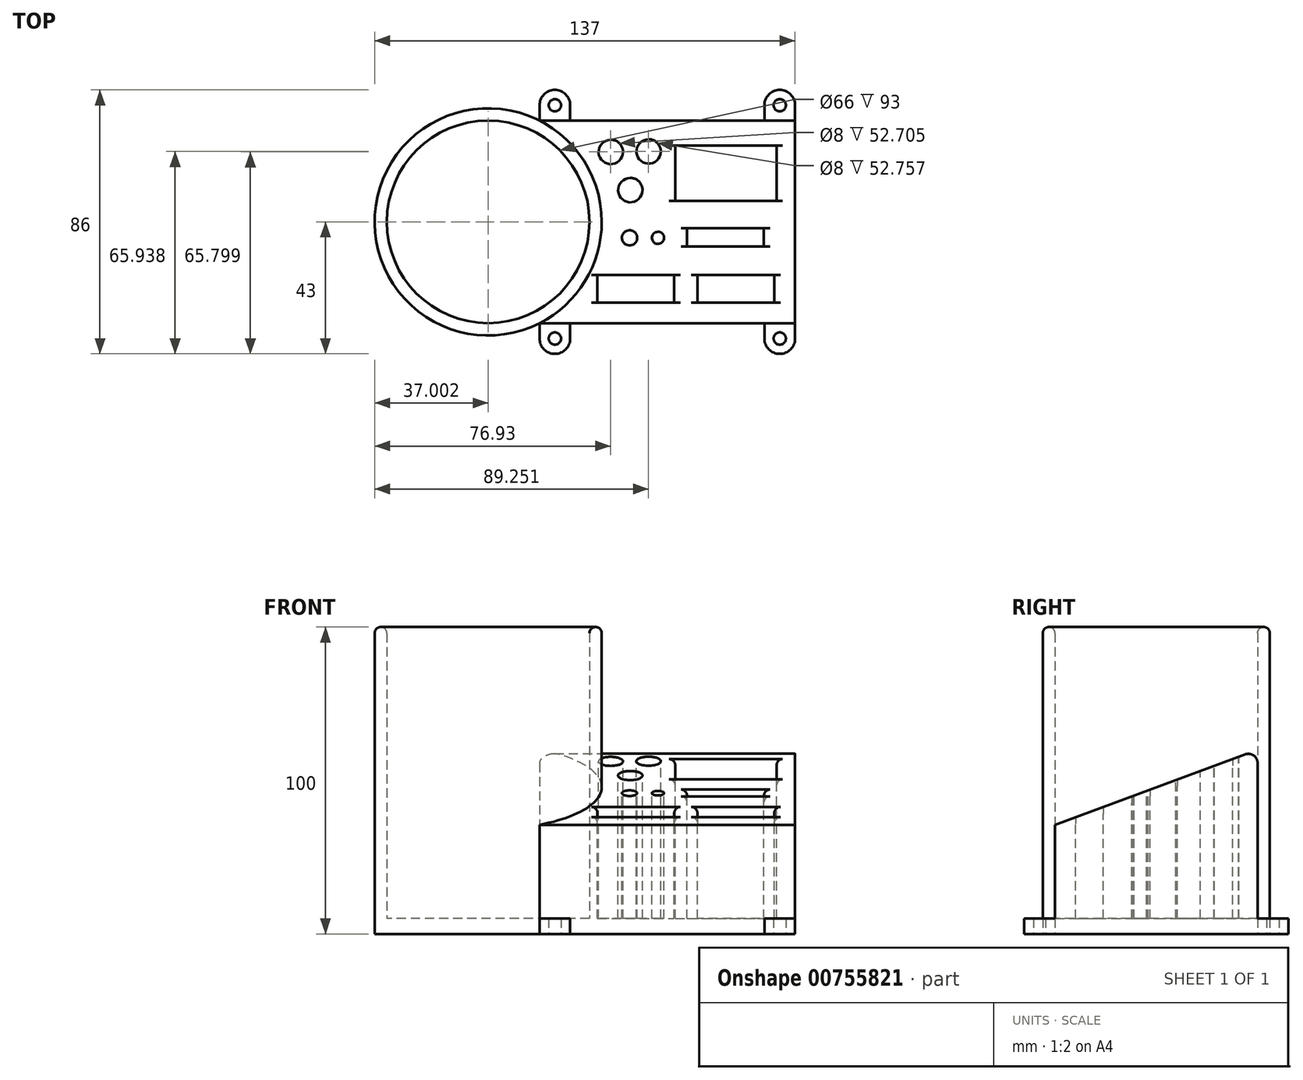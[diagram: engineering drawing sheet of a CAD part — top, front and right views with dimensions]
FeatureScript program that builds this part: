
annotation { "Feature Type Name" : "Feature", "Feature Type Description" : "" }
export const myFeature = defineFeature(function(context is Context, id is Id, definition is map)
    precondition{}
    {
        {
            var Q0;
            Q0=qCreatedBy(makeId("Top.planeOp"),FACE);
            var sketch = newSketch(context, id + "F0", { "sketchPlane" : qUnion([Q0])});
            skCircle(sketch, "E0", {"center": v(-81.99, 0) * mm, "radius": 33 * mm});
            skCircle(sketch, "E1", {"center": v(-81.99, 0) * mm, "radius": 37 * mm});
            skLineSegment(sketch, "E2.bottom", {"start": v(-81.99, 33) * mm, "end": v(18.01, 33) * mm});
            skLineSegment(sketch, "E2.top", {"start": v(-81.99, -33) * mm, "end": v(18.01, -33) * mm});
            skLineSegment(sketch, "E2.left", {"start": v(-81.99, 33) * mm, "end": v(-81.99, -33) * mm});
            skLineSegment(sketch, "E2.right", {"start": v(18.01, 33) * mm, "end": v(18.01, -33) * mm});
            skSolve(sketch);
        }
        {
            var Q0;
            {var subQ1=sQuery(id+"F0.wireOp",EDGE,"E2.bottom");var subQ6=sQuery(id+"F0.wireOp",EDGE,"E1");var subQ7=makeQuery(id+"F0.imprint","INTERSECT",VERTEX,{"derivedFrom":[subQ6,subQ1]});Q0=makeQuery(id+"F0.imprint","IMPRINT",FACE,{"disambiguationData":[TD([[makeQuery(id+"F0.imprint","IMPRINT",EDGE,{"disambiguationData":[TD([[subQ7,-1.0]])],"derivedFrom":subQ6}),1.0]])]});}
            var Q1;
            {var subQ1=sQuery(id+"F0.wireOp",EDGE,"E2.bottom");var subQ6=sQuery(id+"F0.wireOp",EDGE,"E1");var subQ8=makeQuery(id+"F0.imprint","INTERSECT",VERTEX,{"derivedFrom":[subQ6,subQ1]});Q1=makeQuery(id+"F0.imprint","IMPRINT",FACE,{"disambiguationData":[TD([[makeQuery(id+"F0.imprint","IMPRINT",EDGE,{"disambiguationData":[TD([[subQ8,1.0]])],"derivedFrom":subQ6}),1.0]])]});}
            extrude(context, id + "F1", {"entities" : qUnion([Q0, Q1]), "depth" : 100 * mm, "offsetDistance" : 25 * mm});
        }
        {
            var Q0;
            Q0 = qSketchRegion(id + "F0", true);
            extrude(context, id + "F2", {"entities" : qUnion([Q0]), "operationType" : NewBodyOperationType.ADD, "depth" : 60 * mm, "offsetDistance" : 25 * mm});
        }
        {
            var Q0;
            {var subQ0=sQuery(id+"F0.wireOp",EDGE,"E1");var subQ1=sQuery(id+"F0.wireOp",EDGE,"E0");Q0=makeQuery(id+"F2.boolean.opBoolean","MERGE",FACE,{"derivedFrom":[makeQuery(id+"F1.opExtrude","CAP_FACE",FACE,{"disambiguationData":[OSD([subQ1,subQ0])],"isStart":true}),makeQuery(id+"F2.opExtrude","CAP_FACE",FACE,{"disambiguationData":[OSD([subQ1,subQ0,sQuery(id+"F0.wireOp",EDGE,"E2.bottom"),sQuery(id+"F0.wireOp",EDGE,"E2.top"),sQuery(id+"F0.wireOp",EDGE,"E2.right")])],"isStart":true})]});}
            var sketch = newSketch(context, id + "F3", { "sketchPlane" : qUnion([Q0])});
            skCircle(sketch, "E3", {"center": v(-81.99, 0) * mm, "radius": 33 * mm});
            skSolve(sketch);
        }
        {
            var Q0;
            Q0 = qSketchRegion(id + "F3", true);
            extrude(context, id + "F4", {"entities" : qUnion([Q0]), "operationType" : NewBodyOperationType.ADD, "oppositeDirection" : true, "depth" : 5 * mm, "offsetDistance" : 25 * mm});
        }
        {
            var Q0;
            Q0=makeQuery(id+"F2.opExtrude","CAP_FACE",FACE,{"disambiguationData":[OSD([sQuery(id+"F0.wireOp",EDGE,"E0"),sQuery(id+"F0.wireOp",EDGE,"E1"),sQuery(id+"F0.wireOp",EDGE,"E2.bottom"),sQuery(id+"F0.wireOp",EDGE,"E2.top"),sQuery(id+"F0.wireOp",EDGE,"E2.right")])],"isStart":false});
            var sketch = newSketch(context, id + "F5", { "sketchPlane" : qUnion([Q0])});
            skLineSegment(sketch, "E4.bottom", {"start": v(-21.04, 24.86) * mm, "end": v(11.96, 24.86) * mm});
            skLineSegment(sketch, "E4.top", {"start": v(-21.04, 6.86) * mm, "end": v(11.96, 6.86) * mm});
            skLineSegment(sketch, "E4.left", {"start": v(-21.04, 24.86) * mm, "end": v(-21.04, 6.86) * mm});
            skLineSegment(sketch, "E4.right", {"start": v(11.96, 24.86) * mm, "end": v(11.96, 6.86) * mm});
            skCircle(sketch, "E5", {"center": v(-35.93, -5.2) * mm, "radius": 2.5 * mm});
            skCircle(sketch, "E6", {"center": v(-26.66, -5.2) * mm, "radius": 2 * mm});
            skPoint(sketch, "E7.firstSnap0", {"position": v(-4.54, 6.86) * mm});
            skLineSegment(sketch, "E7.right", {"start": v(7.83, -2.02) * mm, "end": v(7.83, -8.02) * mm});
            skLineSegment(sketch, "E8.MirrorCS", {"start": v(-17.17, -2.02) * mm, "end": v(-17.17, -8.02) * mm});
            skLineSegment(sketch, "E9", {"start": v(-17.17, -2.02) * mm, "end": v(7.83, -2.02) * mm});
            skLineSegment(sketch, "E10", {"start": v(-17.17, -8.02) * mm, "end": v(7.83, -8.02) * mm});
            skLineSegment(sketch, "E11.bottom", {"start": v(-46.37, -17.29) * mm, "end": v(-21.37, -17.29) * mm});
            skLineSegment(sketch, "E11.top", {"start": v(-46.37, -26.29) * mm, "end": v(-21.37, -26.29) * mm});
            skLineSegment(sketch, "E11.left", {"start": v(-46.37, -17.29) * mm, "end": v(-46.37, -26.29) * mm});
            skLineSegment(sketch, "E11.right", {"start": v(-21.37, -17.29) * mm, "end": v(-21.37, -26.29) * mm});
            skCircle(sketch, "E12", {"center": v(-42.06, 22.8) * mm, "radius": 4 * mm});
            skCircle(sketch, "E13", {"center": v(-29.74, 22.94) * mm, "radius": 4 * mm});
            skCircle(sketch, "E14", {"center": v(-35.7, 10.35) * mm, "radius": 4 * mm});
            skLineSegment(sketch, "E15.bottom", {"start": v(11.21, -26.29) * mm, "end": v(-13.79, -26.29) * mm});
            skLineSegment(sketch, "E15.top", {"start": v(11.21, -17.29) * mm, "end": v(-13.79, -17.29) * mm});
            skLineSegment(sketch, "E15.left", {"start": v(11.21, -26.29) * mm, "end": v(11.21, -17.29) * mm});
            skLineSegment(sketch, "E15.right", {"start": v(-13.79, -26.29) * mm, "end": v(-13.79, -17.29) * mm});
            skPoint(sketch, "E15.middle", {"position": v(-1.29, -21.79) * mm});
            skPoint(sketch, "E15.middle.positionSnap0", {"position": v(-46.37, -21.79) * mm});
            skPoint(sketch, "E15.cornerSnap0", {"position": v(-33.87, -26.29) * mm});
            skPoint(sketch, "E15.centerSnap0", {"position": v(-46.37, -21.79) * mm});
            skSolve(sketch);
        }
        {
            var Q0;
            Q0 = qSketchRegion(id + "F5", true);
            extrude(context, id + "F6", {"entities" : qUnion([Q0]), "operationType" : NewBodyOperationType.REMOVE, "oppositeDirection" : true, "depth" : 55 * mm, "offsetDistance" : 25 * mm});
        }
        {
            var Q0;
            Q0=makeQuery(id+"F2.opExtrude","SWEPT_FACE",FACE,{"disambiguationData":[OSD([sQuery(id+"F0.wireOp",EDGE,"E2.right")])]});
            var sketch = newSketch(context, id + "F7", { "sketchPlane" : qUnion([Q0])});
            skLineSegment(sketch, "E16", {"start": v(33, 60) * mm, "end": v(-33, 35.57) * mm});
            skLineSegment(sketch, "E17", {"start": v(-33, 35.57) * mm, "end": v(-33, 60) * mm});
            skLineSegment(sketch, "E18", {"start": v(-33, 60) * mm, "end": v(33, 60) * mm});
            skSolve(sketch);
        }
        {
            var Q0;
            Q0 = qSketchRegion(id + "F7", true);
            extrude(context, id + "F8", {"entities" : qUnion([Q0]), "operationType" : NewBodyOperationType.REMOVE, "oppositeDirection" : true, "depth" : 123.5 * mm, "offsetDistance" : 25 * mm});
        }
        {
            var Q0;
            Q0=makeQuery(id+"F1.opExtrude","CAP_FACE",FACE,{"disambiguationData":[OSD([sQuery(id+"F0.wireOp",EDGE,"E0"),sQuery(id+"F0.wireOp",EDGE,"E1")])],"isStart":false});
            extrude(context, id + "F9", {"entities" : qUnion([Q0]), "operationType" : NewBodyOperationType.ADD, "oppositeDirection" : true, "depth" : 100 * mm, "offsetDistance" : 25 * mm});
        }
        {
            var Q0;
            {var subQ0=sQuery(id+"F0.wireOp",EDGE,"E1");var subQ1=sQuery(id+"F0.wireOp",EDGE,"E0");Q0=makeQuery(id+"F4.boolean.opBoolean","MERGE",FACE,{"derivedFrom":[makeQuery(id+"F2.boolean.opBoolean","MERGE",FACE,{"derivedFrom":[makeQuery(id+"F1.opExtrude","CAP_FACE",FACE,{"disambiguationData":[OSD([subQ1,subQ0])],"isStart":true}),makeQuery(id+"F2.opExtrude","CAP_FACE",FACE,{"disambiguationData":[OSD([subQ1,subQ0,sQuery(id+"F0.wireOp",EDGE,"E2.bottom"),sQuery(id+"F0.wireOp",EDGE,"E2.top"),sQuery(id+"F0.wireOp",EDGE,"E2.right")])],"isStart":true})]}),makeQuery(id+"F4.opExtrude","CAP_FACE",FACE,{"disambiguationData":[OSD([sQuery(id+"F3.wireOp",EDGE,"E3")])],"isStart":true})]});}
            var sketch = newSketch(context, id + "F10", { "sketchPlane" : qUnion([Q0])});
            skLineSegment(sketch, "E19.bottom", {"start": v(18.01, 33) * mm, "end": v(8.01, 33) * mm});
            skLineSegment(sketch, "E19.top", {"start": v(18.01, 43) * mm, "end": v(8.01, 43) * mm});
            skLineSegment(sketch, "E19.left", {"start": v(18.01, 33) * mm, "end": v(18.01, 43) * mm});
            skLineSegment(sketch, "E19.right", {"start": v(8.01, 33) * mm, "end": v(8.01, 43) * mm});
            skLineSegment(sketch, "E20.bottom", {"start": v(18.01, -33) * mm, "end": v(8.01, -33) * mm});
            skLineSegment(sketch, "E20.top", {"start": v(18.01, -43) * mm, "end": v(8.01, -43) * mm});
            skLineSegment(sketch, "E20.left", {"start": v(18.01, -33) * mm, "end": v(18.01, -43) * mm});
            skLineSegment(sketch, "E20.right", {"start": v(8.01, -33) * mm, "end": v(8.01, -43) * mm});
            skLineSegment(sketch, "E21.bottom", {"start": v(-65.26, -33) * mm, "end": v(-55.26, -33) * mm});
            skLineSegment(sketch, "E21.top", {"start": v(-65.26, -43) * mm, "end": v(-55.26, -43) * mm});
            skLineSegment(sketch, "E21.left", {"start": v(-65.26, -33) * mm, "end": v(-65.26, -43) * mm});
            skLineSegment(sketch, "E21.right", {"start": v(-55.26, -33) * mm, "end": v(-55.26, -43) * mm});
            skLineSegment(sketch, "E22.bottom", {"start": v(-65.26, 33) * mm, "end": v(-55.26, 33) * mm});
            skLineSegment(sketch, "E22.top", {"start": v(-65.26, 43) * mm, "end": v(-55.26, 43) * mm});
            skLineSegment(sketch, "E22.left", {"start": v(-65.26, 33) * mm, "end": v(-65.26, 43) * mm});
            skLineSegment(sketch, "E22.right", {"start": v(-55.26, 33) * mm, "end": v(-55.26, 43) * mm});
            skCircle(sketch, "E23", {"center": v(-60.26, 38) * mm, "radius": 2 * mm});
            skPoint(sketch, "E23.centerSnap0", {"position": v(-55.26, 38) * mm});
            skPoint(sketch, "E23.centerSnap1", {"position": v(-60.26, 43) * mm});
            skCircle(sketch, "E24", {"center": v(13.01, 38) * mm, "radius": 2 * mm});
            skPoint(sketch, "E24.centerSnap0", {"position": v(13.01, 43) * mm});
            skPoint(sketch, "E24.centerSnap1", {"position": v(-65.26, 38) * mm});
            skCircle(sketch, "E25", {"center": v(13.01, -38) * mm, "radius": 2 * mm});
            skPoint(sketch, "E25.centerSnap0", {"position": v(13.01, -43) * mm});
            skPoint(sketch, "E25.centerSnap1", {"position": v(18.01, -38) * mm});
            skCircle(sketch, "E26", {"center": v(-60.26, -38) * mm, "radius": 2 * mm});
            skPoint(sketch, "E26.centerSnap0", {"position": v(-55.26, -38) * mm});
            skPoint(sketch, "E26.centerSnap1", {"position": v(-60.26, -43) * mm});
            skSolve(sketch);
        }
        {
            var Q0;
            Q0=makeQuery(id+"F1.opExtrude","CAP_EDGE",EDGE,{"disambiguationData":[OSD([sQuery(id+"F0.wireOp",EDGE,"E1")])],"isStart":false});
            var Q1;
            Q1=makeQuery(id+"F1.opExtrude","CAP_EDGE",EDGE,{"disambiguationData":[OSD([sQuery(id+"F0.wireOp",EDGE,"E0")])],"isStart":false});
            fillet(context, id + "F11", {"entities" : qUnion([Q0, Q1]), "radius" : 2 * mm, "tangentPropagation" : true, "allowEdgeOverflow" : false});
        }
        {
            var Q0;
            Q0 = qSketchRegion(id + "F10", true);
            extrude(context, id + "F12", {"entities" : qUnion([Q0]), "operationType" : NewBodyOperationType.ADD, "oppositeDirection" : true, "depth" : 5 * mm, "offsetDistance" : 25 * mm});
        }
        {
            var Q0;
            Q0=makeQuery(id+"F12.opExtrude","SWEPT_EDGE",EDGE,{"disambiguationData":[OSD([sQuery(id+"F10.wireOp",EDGE,"E22.top"),sQuery(id+"F10.wireOp",EDGE,"E22.left")])]});
            var Q1;
            Q1=makeQuery(id+"F12.opExtrude","SWEPT_EDGE",EDGE,{"disambiguationData":[OSD([sQuery(id+"F10.wireOp",EDGE,"E22.top"),sQuery(id+"F10.wireOp",EDGE,"E22.right")])]});
            var Q2;
            Q2=makeQuery(id+"F12.opExtrude","SWEPT_EDGE",EDGE,{"disambiguationData":[OSD([sQuery(id+"F10.wireOp",EDGE,"E19.top"),sQuery(id+"F10.wireOp",EDGE,"E19.right")])]});
            var Q3;
            Q3=makeQuery(id+"F12.opExtrude","SWEPT_EDGE",EDGE,{"disambiguationData":[OSD([sQuery(id+"F10.wireOp",EDGE,"E19.top"),sQuery(id+"F10.wireOp",EDGE,"E19.left")])]});
            var Q4;
            Q4=makeQuery(id+"F12.opExtrude","SWEPT_EDGE",EDGE,{"disambiguationData":[OSD([sQuery(id+"F10.wireOp",EDGE,"E20.top"),sQuery(id+"F10.wireOp",EDGE,"E20.left")])]});
            var Q5;
            Q5=makeQuery(id+"F12.opExtrude","SWEPT_EDGE",EDGE,{"disambiguationData":[OSD([sQuery(id+"F10.wireOp",EDGE,"E20.top"),sQuery(id+"F10.wireOp",EDGE,"E20.right")])]});
            var Q6;
            Q6=makeQuery(id+"F12.opExtrude","SWEPT_EDGE",EDGE,{"disambiguationData":[OSD([sQuery(id+"F10.wireOp",EDGE,"E21.top"),sQuery(id+"F10.wireOp",EDGE,"E21.right")])]});
            var Q7;
            Q7=makeQuery(id+"F12.opExtrude","SWEPT_EDGE",EDGE,{"disambiguationData":[OSD([sQuery(id+"F10.wireOp",EDGE,"E21.top"),sQuery(id+"F10.wireOp",EDGE,"E21.left")])]});
            fillet(context, id + "F13", {"entities" : qUnion([Q0, Q1, Q2, Q3, Q4, Q5, Q6, Q7]), "radius" : 5 * mm, "tangentPropagation" : true, "allowEdgeOverflow" : false});
        }
        {
            var Q0;
            Q0=makeQuery(id+"F8.boolean.opBoolean","INTERSECT",EDGE,{"derivedFrom":[makeQuery(id+"F6.boolean.opBoolean","COPY",FACE,{"derivedFrom":makeQuery(id+"F6.opExtrude","SWEPT_FACE",FACE,{"disambiguationData":[OSD([sQuery(id+"F5.wireOp",EDGE,"E4.left")])]})}),makeQuery(id+"F8.opExtrude","SWEPT_FACE",FACE,{"disambiguationData":[OSD([sQuery(id+"F7.wireOp",EDGE,"E16")])]})]});
            var Q1;
            Q1=makeQuery(id+"F8.boolean.opBoolean","INTERSECT",EDGE,{"derivedFrom":[makeQuery(id+"F6.boolean.opBoolean","COPY",FACE,{"derivedFrom":makeQuery(id+"F6.opExtrude","SWEPT_FACE",FACE,{"disambiguationData":[OSD([sQuery(id+"F5.wireOp",EDGE,"E4.right")])]})}),makeQuery(id+"F8.opExtrude","SWEPT_FACE",FACE,{"disambiguationData":[OSD([sQuery(id+"F7.wireOp",EDGE,"E16")])]})]});
            var Q2;
            Q2=makeQuery(id+"F8.boolean.opBoolean","INTERSECT",EDGE,{"derivedFrom":[makeQuery(id+"F6.boolean.opBoolean","COPY",FACE,{"derivedFrom":makeQuery(id+"F6.opExtrude","SWEPT_FACE",FACE,{"disambiguationData":[OSD([sQuery(id+"F5.wireOp",EDGE,"E7.right")])]})}),makeQuery(id+"F8.opExtrude","SWEPT_FACE",FACE,{"disambiguationData":[OSD([sQuery(id+"F7.wireOp",EDGE,"E16")])]})]});
            var Q3;
            Q3=makeQuery(id+"F8.boolean.opBoolean","INTERSECT",EDGE,{"derivedFrom":[makeQuery(id+"F6.boolean.opBoolean","COPY",FACE,{"derivedFrom":makeQuery(id+"F6.opExtrude","SWEPT_FACE",FACE,{"disambiguationData":[OSD([sQuery(id+"F5.wireOp",EDGE,"E8.MirrorCS")])]})}),makeQuery(id+"F8.opExtrude","SWEPT_FACE",FACE,{"disambiguationData":[OSD([sQuery(id+"F7.wireOp",EDGE,"E16")])]})]});
            var Q4;
            Q4=makeQuery(id+"F8.boolean.opBoolean","INTERSECT",EDGE,{"derivedFrom":[makeQuery(id+"F6.boolean.opBoolean","COPY",FACE,{"derivedFrom":makeQuery(id+"F6.opExtrude","SWEPT_FACE",FACE,{"disambiguationData":[OSD([sQuery(id+"F5.wireOp",EDGE,"E11.right")])]})}),makeQuery(id+"F8.opExtrude","SWEPT_FACE",FACE,{"disambiguationData":[OSD([sQuery(id+"F7.wireOp",EDGE,"E16")])]})]});
            var Q5;
            Q5=makeQuery(id+"F8.boolean.opBoolean","INTERSECT",EDGE,{"derivedFrom":[makeQuery(id+"F6.boolean.opBoolean","COPY",FACE,{"derivedFrom":makeQuery(id+"F6.opExtrude","SWEPT_FACE",FACE,{"disambiguationData":[OSD([sQuery(id+"F5.wireOp",EDGE,"E11.left")])]})}),makeQuery(id+"F8.opExtrude","SWEPT_FACE",FACE,{"disambiguationData":[OSD([sQuery(id+"F7.wireOp",EDGE,"E16")])]})]});
            var Q6;
            Q6=makeQuery(id+"F8.boolean.opBoolean","INTERSECT",EDGE,{"derivedFrom":[makeQuery(id+"F6.boolean.opBoolean","COPY",FACE,{"derivedFrom":makeQuery(id+"F6.opExtrude","SWEPT_FACE",FACE,{"disambiguationData":[OSD([sQuery(id+"F5.wireOp",EDGE,"E15.left")])]})}),makeQuery(id+"F8.opExtrude","SWEPT_FACE",FACE,{"disambiguationData":[OSD([sQuery(id+"F7.wireOp",EDGE,"E16")])]})]});
            var Q7;
            Q7=makeQuery(id+"F8.boolean.opBoolean","INTERSECT",EDGE,{"derivedFrom":[makeQuery(id+"F6.boolean.opBoolean","COPY",FACE,{"derivedFrom":makeQuery(id+"F6.opExtrude","SWEPT_FACE",FACE,{"disambiguationData":[OSD([sQuery(id+"F5.wireOp",EDGE,"E15.right")])]})}),makeQuery(id+"F8.opExtrude","SWEPT_FACE",FACE,{"disambiguationData":[OSD([sQuery(id+"F7.wireOp",EDGE,"E16")])]})]});
            fillet(context, id + "F14", {"entities" : qUnion([Q0, Q1, Q2, Q3, Q4, Q5, Q6, Q7]), "radius" : 2 * mm, "tangentPropagation" : true, "allowEdgeOverflow" : false});
        }
        {
            var Q0;
            {var subQ0=sQuery(id+"F0.wireOp",EDGE,"E2.bottom");Q0=makeQuery(id+"F8.boolean.opBoolean","MERGE",EDGE,{"derivedFrom":[makeQuery(id+"F2.opExtrude","CAP_EDGE",EDGE,{"disambiguationData":[OSD([subQ0])],"isStart":false}),makeQuery(id+"F8.opExtrude","SWEPT_EDGE",EDGE,{"disambiguationData":[OSD([subQ0,sQuery(id+"F0.wireOp",EDGE,"E2.right"),sQuery(id+"F7.wireOp",EDGE,"E16"),sQuery(id+"F7.wireOp",EDGE,"E18")])]})]});}
            var Q1;
            {var subQ0=sQuery(id+"F0.wireOp",EDGE,"E2.top");var subQ1=sQuery(id+"F7.wireOp",EDGE,"E16");Q1=makeQuery(id+"F8.boolean.opBoolean","COPY",EDGE,{"disambiguationData":[topologyDisambiguationEdgeConnected([makeQuery(id+"F2.opExtrude","SWEPT_FACE",FACE,{"disambiguationData":[OSD([subQ0])]}),makeQuery(id+"F8.opExtrude","SWEPT_FACE",FACE,{"disambiguationData":[OSD([subQ1])]})])],"derivedFrom":makeQuery(id+"F8.opExtrude","SWEPT_EDGE",EDGE,{"disambiguationData":[OSD([subQ0,sQuery(id+"F0.wireOp",EDGE,"E2.right"),subQ1,sQuery(id+"F7.wireOp",EDGE,"E17")])]})});}
            var Q2;
            Q2=makeQuery(id+"F8.boolean.opBoolean","COPY",EDGE,{"derivedFrom":makeQuery(id+"F8.opExtrude","CAP_EDGE",EDGE,{"disambiguationData":[OSD([sQuery(id+"F7.wireOp",EDGE,"E16")])],"isStart":true})});
            fillet(context, id + "F15", {"entities" : qUnion([Q0, Q1, Q2]), "radius" : 3 * mm, "tangentPropagation" : true, "allowEdgeOverflow" : false});
        }
    });
